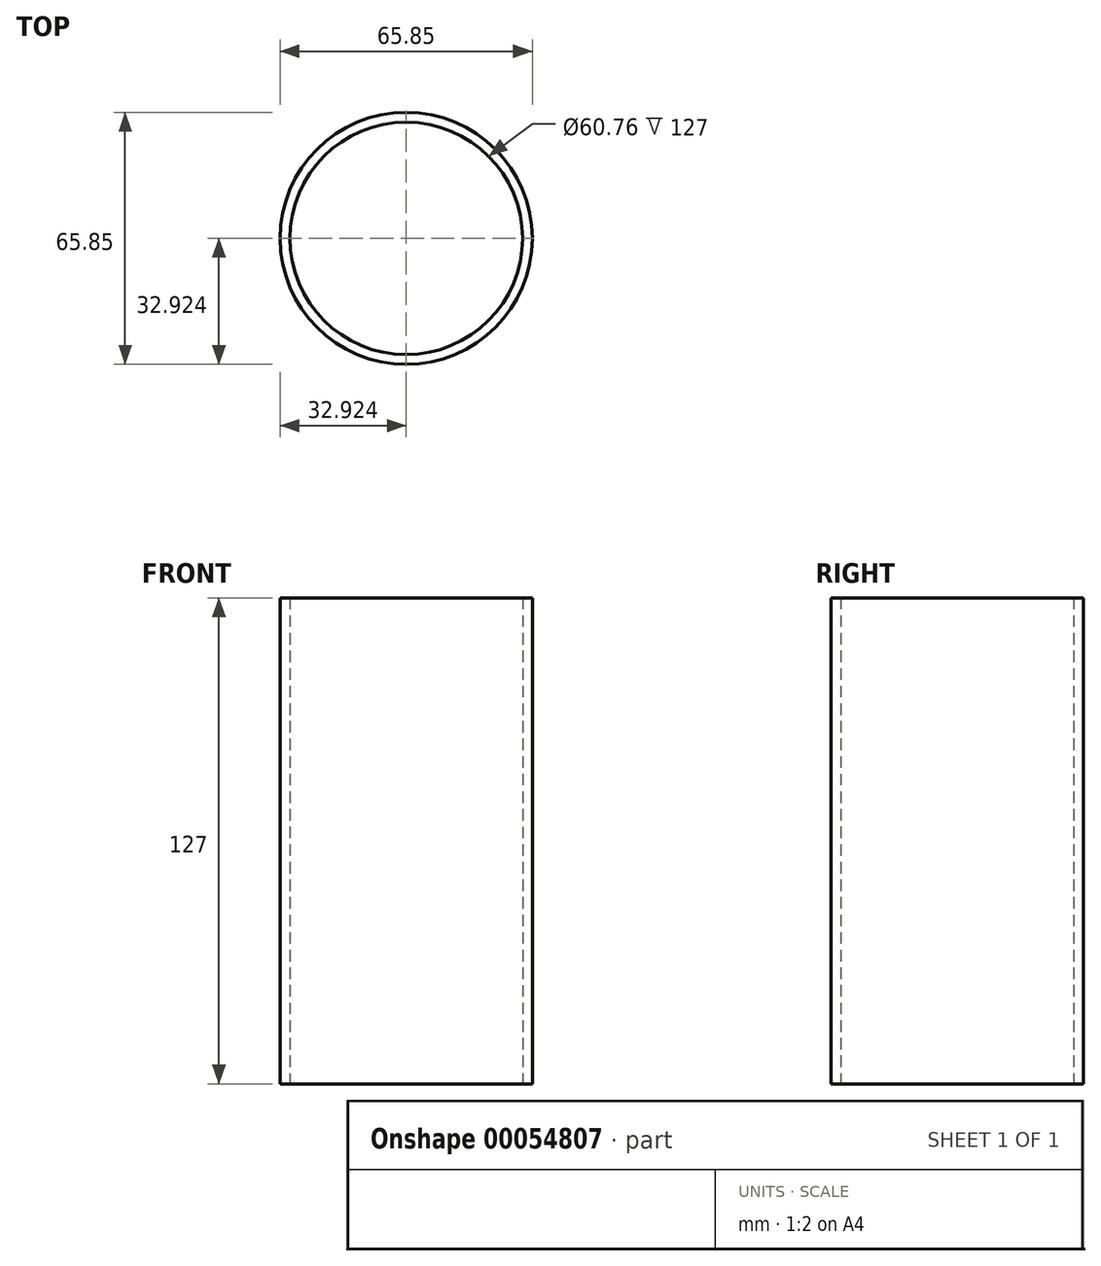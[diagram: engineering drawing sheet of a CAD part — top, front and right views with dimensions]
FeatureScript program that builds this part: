
annotation { "Feature Type Name" : "Feature", "Feature Type Description" : "" }
export const myFeature = defineFeature(function(context is Context, id is Id, definition is map)
    precondition{}
    {
        {
            var Q0;
            Q0=qCreatedBy(makeId("Top.planeOp"),FACE);
            var sketch = newSketch(context, id + "F0", { "sketchPlane" : qUnion([Q0])});
            skCircle(sketch, "E0", {"center": v(-2.02, 3.02) * mm, "radius": 32.92 * mm});
            skSolve(sketch);
        }
        {
            var Q0;
            Q0=makeQuery(id+"F0.imprint","IMPRINT",FACE,{"disambiguationData":[TD([[makeQuery(id+"F0.imprint","IMPRINT",EDGE,{"derivedFrom":sQuery(id+"F0.wireOp",EDGE,"E0")}),1.0]])]});
            extrude(context, id + "F1", {"entities" : qUnion([Q0]), "depth" : 127 * mm});
        }
        {
            var Q0;
            Q0=makeQuery(id+"F1.opExtrude","CAP_FACE",FACE,{"disambiguationData":[OSD([sQuery(id+"F0.wireOp",EDGE,"E0")])],"isStart":false});
            var Q1;
            Q1=makeQuery(id+"F1.opExtrude","CAP_FACE",FACE,{"disambiguationData":[OSD([sQuery(id+"F0.wireOp",EDGE,"E0")])],"isStart":true});
            shell(context, id + "F2", {"entities" : qUnion([Q0, Q1]), "thickness" : 2.54 * mm});
        }
    });
